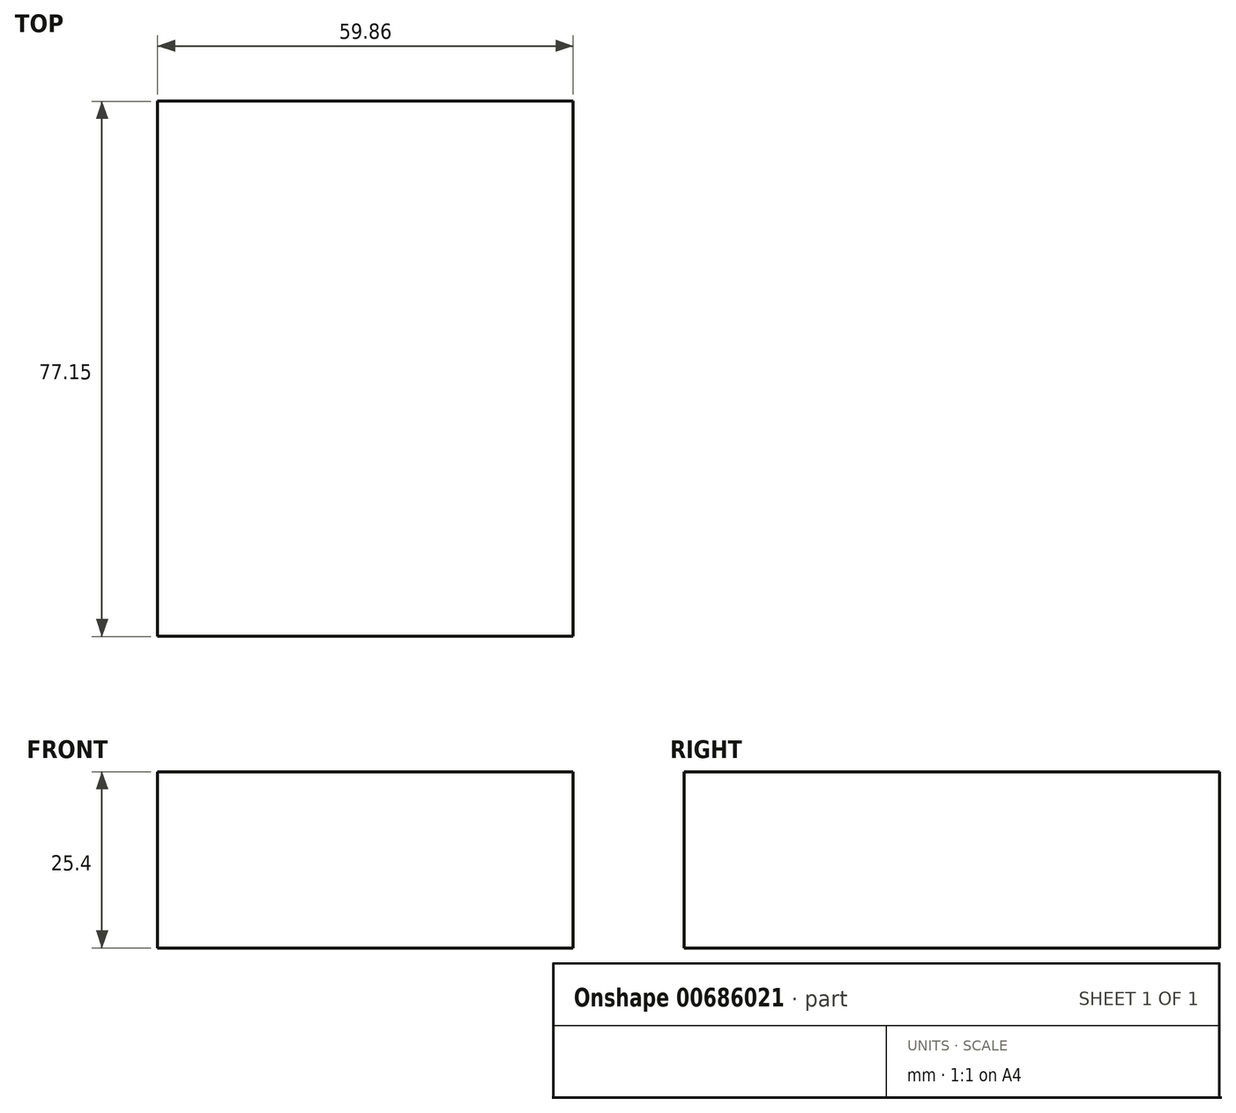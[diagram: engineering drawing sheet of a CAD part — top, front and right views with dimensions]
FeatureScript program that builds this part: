
annotation { "Feature Type Name" : "Feature", "Feature Type Description" : "" }
export const myFeature = defineFeature(function(context is Context, id is Id, definition is map)
    precondition{}
    {
        {
            var Q0;
            Q0=qCreatedBy(makeId("Top.planeOp"),FACE);
            var sketch = newSketch(context, id + "F0", { "sketchPlane" : qUnion([Q0])});
            skLineSegment(sketch, "E0.bottom", {"start": v(42.16, -33.4) * mm, "end": v(-17.7, -33.4) * mm});
            skLineSegment(sketch, "E0.top", {"start": v(42.16, 43.75) * mm, "end": v(-17.7, 43.75) * mm});
            skLineSegment(sketch, "E0.left", {"start": v(42.16, -33.4) * mm, "end": v(42.16, 43.75) * mm});
            skLineSegment(sketch, "E0.right", {"start": v(-17.7, -33.4) * mm, "end": v(-17.7, 43.75) * mm});
            skSolve(sketch);
        }
        {
            var Q0;
            Q0=makeQuery(id+"F0.imprint","IMPRINT",FACE,{"disambiguationData":[TD([[makeQuery(id+"F0.imprint","IMPRINT",EDGE,{"derivedFrom":sQuery(id+"F0.wireOp",EDGE,"E0.bottom")}),-1.0]])]});
            extrude(context, id + "F1", {"entities" : qUnion([Q0]), "depth" : 25.4 * mm, "offsetDistance" : 25.4 * mm});
        }
    });
